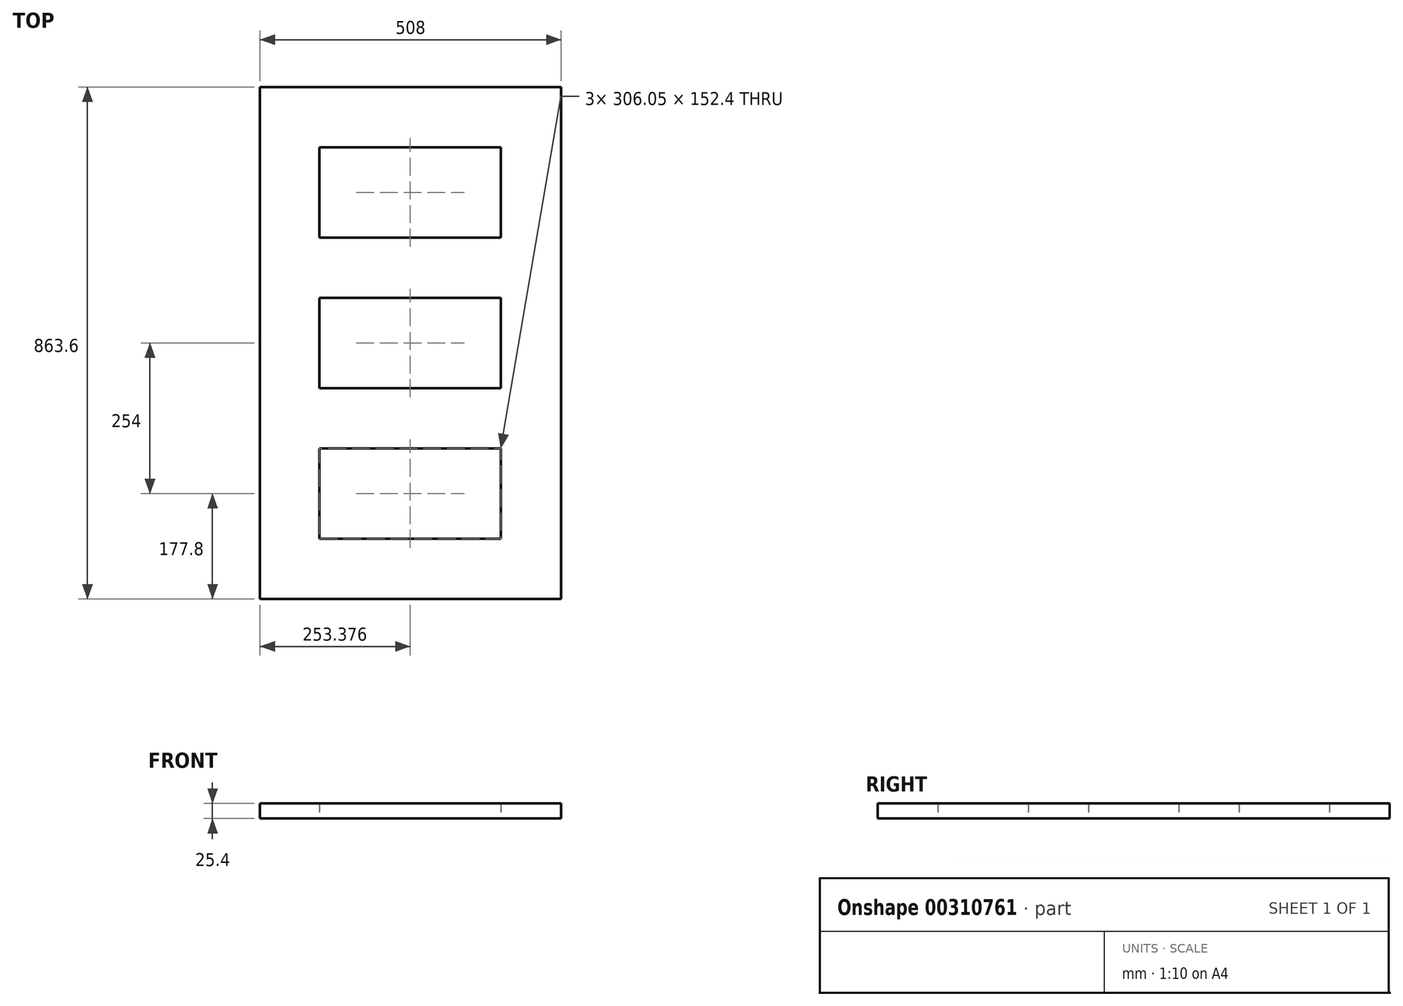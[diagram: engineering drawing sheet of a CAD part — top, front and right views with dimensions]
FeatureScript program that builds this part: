
annotation { "Feature Type Name" : "Feature", "Feature Type Description" : "" }
export const myFeature = defineFeature(function(context is Context, id is Id, definition is map)
    precondition{}
    {
        {
            var Q0;
            Q0=qCreatedBy(makeId("Top.planeOp"),FACE);
            var sketch = newSketch(context, id + "F0", { "sketchPlane" : qUnion([Q0])});
            skLineSegment(sketch, "E0.bottom", {"start": v(-32.43, 871.42) * mm, "end": v(475.57, 871.42) * mm});
            skLineSegment(sketch, "E0.top", {"start": v(-32.43, 7.82) * mm, "end": v(475.57, 7.82) * mm});
            skLineSegment(sketch, "E0.left", {"start": v(-32.43, 871.42) * mm, "end": v(-32.43, 7.82) * mm});
            skLineSegment(sketch, "E0.right", {"start": v(475.57, 871.42) * mm, "end": v(475.57, 7.82) * mm});
            skLineSegment(sketch, "E1.bottom", {"start": v(-32.43, 109.42) * mm, "end": v(475.57, 109.42) * mm});
            skLineSegment(sketch, "E1.top", {"start": v(-32.43, 261.82) * mm, "end": v(475.57, 261.82) * mm});
            skLineSegment(sketch, "E1.left", {"start": v(-32.43, 109.42) * mm, "end": v(-32.43, 261.82) * mm});
            skLineSegment(sketch, "E1.right", {"start": v(475.57, 109.42) * mm, "end": v(475.57, 261.82) * mm});
            skLineSegment(sketch, "E2.bottom", {"start": v(-32.43, 363.42) * mm, "end": v(475.57, 363.42) * mm});
            skLineSegment(sketch, "E2.top", {"start": v(-32.43, 515.82) * mm, "end": v(475.57, 515.82) * mm});
            skLineSegment(sketch, "E2.left", {"start": v(-32.43, 363.42) * mm, "end": v(-32.43, 515.82) * mm});
            skLineSegment(sketch, "E2.right", {"start": v(475.57, 363.42) * mm, "end": v(475.57, 515.82) * mm});
            skLineSegment(sketch, "E3.bottom", {"start": v(-32.43, 617.42) * mm, "end": v(475.57, 617.42) * mm});
            skLineSegment(sketch, "E3.top", {"start": v(-32.43, 769.82) * mm, "end": v(475.57, 769.82) * mm});
            skLineSegment(sketch, "E3.left", {"start": v(-32.43, 617.42) * mm, "end": v(-32.43, 769.82) * mm});
            skLineSegment(sketch, "E3.right", {"start": v(475.57, 617.42) * mm, "end": v(475.57, 769.82) * mm});
            skLineSegment(sketch, "E4.bottom", {"start": v(475.57, 871.42) * mm, "end": v(373.97, 871.42) * mm});
            skLineSegment(sketch, "E4.top", {"start": v(475.57, 7.82) * mm, "end": v(373.97, 7.82) * mm});
            skLineSegment(sketch, "E4.right", {"start": v(373.97, 871.42) * mm, "end": v(373.97, 7.82) * mm});
            skLineSegment(sketch, "E5.bottom", {"start": v(-32.43, 871.42) * mm, "end": v(67.92, 871.42) * mm});
            skLineSegment(sketch, "E5.top", {"start": v(-32.43, 7.82) * mm, "end": v(67.92, 7.82) * mm});
            skLineSegment(sketch, "E5.right", {"start": v(67.92, 871.42) * mm, "end": v(67.92, 7.82) * mm});
            skSolve(sketch);
        }
        {
            var Q0;
            {var subQ0=sQuery(id+"F0.wireOp",EDGE,"E5.right");var subQ1=sQuery(id+"F0.wireOp",EDGE,"E0.bottom");var subQ2=makeQuery(id+"F0.imprint","INTERSECT",VERTEX,{"derivedFrom":[subQ1,subQ0]});Q0=makeQuery(id+"F0.imprint","IMPRINT",FACE,{"disambiguationData":[TD([[makeQuery(id+"F0.imprint","IMPRINT",EDGE,{"disambiguationData":[TD([[subQ2,-1.0]])],"derivedFrom":subQ1}),-1.0]])]});}
            var Q1;
            {var subQ0=sQuery(id+"F0.wireOp",EDGE,"E5.right");var subQ1=sQuery(id+"F0.wireOp",EDGE,"E2.top");var subQ2=makeQuery(id+"F0.imprint","INTERSECT",VERTEX,{"derivedFrom":[subQ1,subQ0]});Q1=makeQuery(id+"F0.imprint","IMPRINT",FACE,{"disambiguationData":[TD([[makeQuery(id+"F0.imprint","IMPRINT",EDGE,{"disambiguationData":[TD([[subQ2,-1.0]])],"derivedFrom":subQ1}),1.0]])]});}
            var Q2;
            {var subQ0=sQuery(id+"F0.wireOp",EDGE,"E5.right");var subQ1=sQuery(id+"F0.wireOp",EDGE,"E1.top");var subQ2=makeQuery(id+"F0.imprint","INTERSECT",VERTEX,{"derivedFrom":[subQ1,subQ0]});Q2=makeQuery(id+"F0.imprint","IMPRINT",FACE,{"disambiguationData":[TD([[makeQuery(id+"F0.imprint","IMPRINT",EDGE,{"disambiguationData":[TD([[subQ2,-1.0]])],"derivedFrom":subQ1}),1.0]])]});}
            var Q3;
            {var subQ0=sQuery(id+"F0.wireOp",EDGE,"E5.right");var subQ1=sQuery(id+"F0.wireOp",EDGE,"E0.top");var subQ2=makeQuery(id+"F0.imprint","INTERSECT",VERTEX,{"derivedFrom":[subQ1,subQ0]});Q3=makeQuery(id+"F0.imprint","IMPRINT",FACE,{"disambiguationData":[TD([[makeQuery(id+"F0.imprint","IMPRINT",EDGE,{"disambiguationData":[TD([[subQ2,-1.0]])],"derivedFrom":subQ1}),1.0]])]});}
            var Q4;
            {var subQ0=sQuery(id+"F0.wireOp",EDGE,"E0.right");var subQ1=sQuery(id+"F0.wireOp",EDGE,"E0.top");var subQ2=makeQuery(id+"F0.imprint","INTERSECT",VERTEX,{"derivedFrom":[subQ1,subQ0]});Q4=makeQuery(id+"F0.imprint","IMPRINT",FACE,{"disambiguationData":[TD([[makeQuery(id+"F0.imprint","IMPRINT",EDGE,{"disambiguationData":[TD([[subQ2,1.0]])],"derivedFrom":subQ1}),1.0]])]});}
            var Q5;
            {var subQ0=sQuery(id+"F0.wireOp",EDGE,"E1.top");var subQ1=sQuery(id+"F0.wireOp",EDGE,"E0.right");var subQ2=makeQuery(id+"F0.imprint","INTERSECT",VERTEX,{"derivedFrom":[subQ1,subQ0]});Q5=makeQuery(id+"F0.imprint","IMPRINT",FACE,{"disambiguationData":[TD([[makeQuery(id+"F0.imprint","IMPRINT",EDGE,{"disambiguationData":[TD([[subQ2,-1.0]])],"derivedFrom":subQ1}),-1.0]])]});}
            var Q6;
            {var subQ0=sQuery(id+"F0.wireOp",EDGE,"E1.top");var subQ1=sQuery(id+"F0.wireOp",EDGE,"E0.right");var subQ2=makeQuery(id+"F0.imprint","INTERSECT",VERTEX,{"derivedFrom":[subQ1,subQ0]});Q6=makeQuery(id+"F0.imprint","IMPRINT",FACE,{"disambiguationData":[TD([[makeQuery(id+"F0.imprint","IMPRINT",EDGE,{"disambiguationData":[TD([[subQ2,1.0]])],"derivedFrom":subQ1}),-1.0]])]});}
            var Q7;
            {var subQ0=sQuery(id+"F0.wireOp",EDGE,"E2.top");var subQ1=sQuery(id+"F0.wireOp",EDGE,"E0.right");var subQ2=makeQuery(id+"F0.imprint","INTERSECT",VERTEX,{"derivedFrom":[subQ1,subQ0]});Q7=makeQuery(id+"F0.imprint","IMPRINT",FACE,{"disambiguationData":[TD([[makeQuery(id+"F0.imprint","IMPRINT",EDGE,{"disambiguationData":[TD([[subQ2,-1.0]])],"derivedFrom":subQ1}),-1.0]])]});}
            var Q8;
            {var subQ0=sQuery(id+"F0.wireOp",EDGE,"E3.bottom");var subQ1=sQuery(id+"F0.wireOp",EDGE,"E0.right");var subQ2=makeQuery(id+"F0.imprint","INTERSECT",VERTEX,{"derivedFrom":[subQ1,subQ0]});Q8=makeQuery(id+"F0.imprint","IMPRINT",FACE,{"disambiguationData":[TD([[makeQuery(id+"F0.imprint","IMPRINT",EDGE,{"disambiguationData":[TD([[subQ2,-1.0]])],"derivedFrom":subQ1}),-1.0]])]});}
            var Q9;
            {var subQ0=sQuery(id+"F0.wireOp",EDGE,"E3.top");var subQ1=sQuery(id+"F0.wireOp",EDGE,"E0.right");var subQ2=makeQuery(id+"F0.imprint","INTERSECT",VERTEX,{"derivedFrom":[subQ1,subQ0]});Q9=makeQuery(id+"F0.imprint","IMPRINT",FACE,{"disambiguationData":[TD([[makeQuery(id+"F0.imprint","IMPRINT",EDGE,{"disambiguationData":[TD([[subQ2,-1.0]])],"derivedFrom":subQ1}),-1.0]])]});}
            var Q10;
            {var subQ0=sQuery(id+"F0.wireOp",EDGE,"E0.right");var subQ1=sQuery(id+"F0.wireOp",EDGE,"E0.bottom");var subQ2=makeQuery(id+"F0.imprint","INTERSECT",VERTEX,{"derivedFrom":[subQ1,subQ0]});Q10=makeQuery(id+"F0.imprint","IMPRINT",FACE,{"disambiguationData":[TD([[makeQuery(id+"F0.imprint","IMPRINT",EDGE,{"disambiguationData":[TD([[subQ2,1.0]])],"derivedFrom":subQ1}),-1.0]])]});}
            var Q11;
            {var subQ0=sQuery(id+"F0.wireOp",EDGE,"E5.right");var subQ1=sQuery(id+"F0.wireOp",EDGE,"E0.bottom");var subQ2=makeQuery(id+"F0.imprint","INTERSECT",VERTEX,{"derivedFrom":[subQ1,subQ0]});Q11=makeQuery(id+"F0.imprint","IMPRINT",FACE,{"disambiguationData":[TD([[makeQuery(id+"F0.imprint","IMPRINT",EDGE,{"disambiguationData":[TD([[subQ2,1.0]])],"derivedFrom":subQ1}),-1.0]])]});}
            var Q12;
            {var subQ0=sQuery(id+"F0.wireOp",EDGE,"E3.top");var subQ1=sQuery(id+"F0.wireOp",EDGE,"E0.left");var subQ2=makeQuery(id+"F0.imprint","INTERSECT",VERTEX,{"derivedFrom":[subQ1,subQ0]});Q12=makeQuery(id+"F0.imprint","IMPRINT",FACE,{"disambiguationData":[TD([[makeQuery(id+"F0.imprint","IMPRINT",EDGE,{"disambiguationData":[TD([[subQ2,-1.0]])],"derivedFrom":subQ1}),1.0]])]});}
            var Q13;
            {var subQ0=sQuery(id+"F0.wireOp",EDGE,"E3.bottom");var subQ1=sQuery(id+"F0.wireOp",EDGE,"E0.left");var subQ2=makeQuery(id+"F0.imprint","INTERSECT",VERTEX,{"derivedFrom":[subQ1,subQ0]});Q13=makeQuery(id+"F0.imprint","IMPRINT",FACE,{"disambiguationData":[TD([[makeQuery(id+"F0.imprint","IMPRINT",EDGE,{"disambiguationData":[TD([[subQ2,-1.0]])],"derivedFrom":subQ1}),1.0]])]});}
            var Q14;
            {var subQ0=sQuery(id+"F0.wireOp",EDGE,"E2.top");var subQ1=sQuery(id+"F0.wireOp",EDGE,"E0.left");var subQ2=makeQuery(id+"F0.imprint","INTERSECT",VERTEX,{"derivedFrom":[subQ1,subQ0]});Q14=makeQuery(id+"F0.imprint","IMPRINT",FACE,{"disambiguationData":[TD([[makeQuery(id+"F0.imprint","IMPRINT",EDGE,{"disambiguationData":[TD([[subQ2,-1.0]])],"derivedFrom":subQ1}),1.0]])]});}
            var Q15;
            {var subQ0=sQuery(id+"F0.wireOp",EDGE,"E2.bottom");var subQ1=sQuery(id+"F0.wireOp",EDGE,"E0.left");var subQ2=makeQuery(id+"F0.imprint","INTERSECT",VERTEX,{"derivedFrom":[subQ1,subQ0]});Q15=makeQuery(id+"F0.imprint","IMPRINT",FACE,{"disambiguationData":[TD([[makeQuery(id+"F0.imprint","IMPRINT",EDGE,{"disambiguationData":[TD([[subQ2,-1.0]])],"derivedFrom":subQ1}),1.0]])]});}
            var Q16;
            {var subQ0=sQuery(id+"F0.wireOp",EDGE,"E1.top");var subQ1=sQuery(id+"F0.wireOp",EDGE,"E0.left");var subQ2=makeQuery(id+"F0.imprint","INTERSECT",VERTEX,{"derivedFrom":[subQ1,subQ0]});Q16=makeQuery(id+"F0.imprint","IMPRINT",FACE,{"disambiguationData":[TD([[makeQuery(id+"F0.imprint","IMPRINT",EDGE,{"disambiguationData":[TD([[subQ2,-1.0]])],"derivedFrom":subQ1}),1.0]])]});}
            var Q17;
            {var subQ0=sQuery(id+"F0.wireOp",EDGE,"E5.right");var subQ1=sQuery(id+"F0.wireOp",EDGE,"E0.top");var subQ2=makeQuery(id+"F0.imprint","INTERSECT",VERTEX,{"derivedFrom":[subQ1,subQ0]});Q17=makeQuery(id+"F0.imprint","IMPRINT",FACE,{"disambiguationData":[TD([[makeQuery(id+"F0.imprint","IMPRINT",EDGE,{"disambiguationData":[TD([[subQ2,1.0]])],"derivedFrom":subQ1}),1.0]])]});}
            extrude(context, id + "F1", {"entities" : qUnion([Q0, Q1, Q2, Q3, Q4, Q5, Q6, Q7, Q8, Q9, Q10, Q11, Q12, Q13, Q14, Q15, Q16, Q17]), "depth" : 25.4 * mm, "offsetDistance" : 25.4 * mm});
        }
    });
